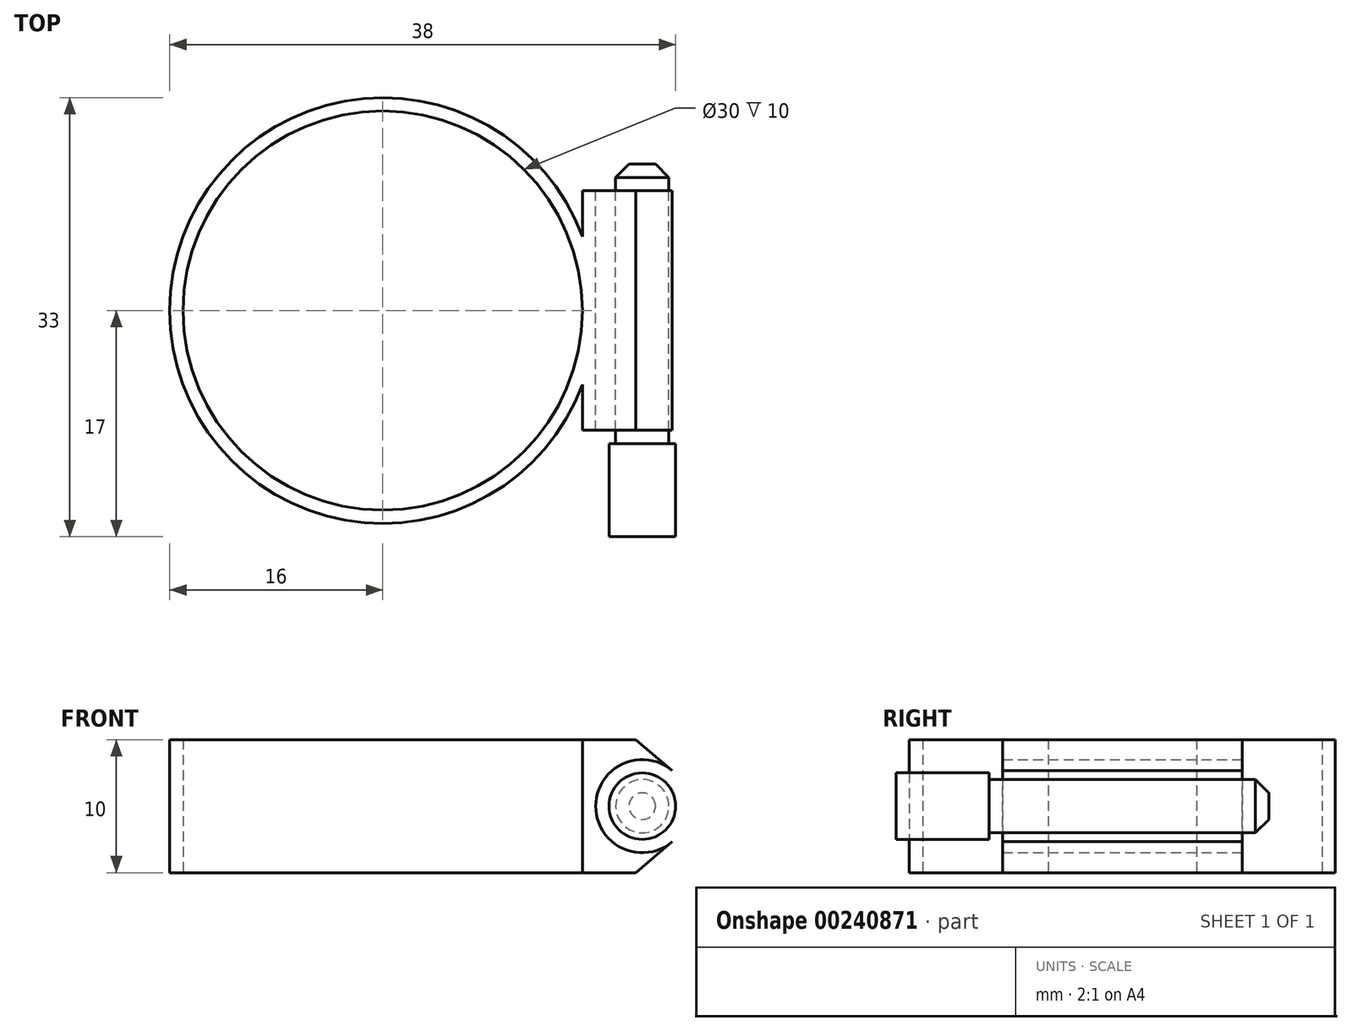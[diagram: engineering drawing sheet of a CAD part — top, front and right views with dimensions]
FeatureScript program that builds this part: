
annotation { "Feature Type Name" : "Feature", "Feature Type Description" : "" }
export const myFeature = defineFeature(function(context is Context, id is Id, definition is map)
    precondition{}
    {
        {
            var Q0;
            Q0=qCreatedBy(makeId("Front.planeOp"),FACE);
            var sketch = newSketch(context, id + "F0", { "sketchPlane" : qUnion([Q0])});
            skLineSegment(sketch, "E0.bottom", {"start": v(15, 0) * mm, "end": v(16, 0) * mm});
            skLineSegment(sketch, "E0.top", {"start": v(15, 10) * mm, "end": v(16, 10) * mm});
            skLineSegment(sketch, "E0.left", {"start": v(15, 0) * mm, "end": v(15, 10) * mm});
            skLineSegment(sketch, "E0.right", {"start": v(16, 0) * mm, "end": v(16, 10) * mm});
            skLineSegment(sketch, "E1", {"start": v(15, 5) * mm, "end": v(23, 5) * mm, "construction": true});
            skCircle(sketch, "E2", {"center": v(19.5, 5) * mm, "radius": 3.5 * mm});
            skLineSegment(sketch, "E3", {"start": v(16, 10) * mm, "end": v(19, 10) * mm});
            skLineSegment(sketch, "E4", {"start": v(19, 10) * mm, "end": v(21.76, 7.68) * mm});
            skPoint(sketch, "E5", {"position": v(16, 5) * mm});
            skLineSegment(sketch, "E6.MirrorCS", {"start": v(16, 0) * mm, "end": v(19, 0) * mm});
            skLineSegment(sketch, "E7.MirrorCS", {"start": v(19, 0) * mm, "end": v(21.76, 2.32) * mm});
            skLineSegment(sketch, "E8", {"start": v(0, 0) * mm, "end": v(0, 10) * mm, "construction": true});
            skSolve(sketch);
        }
        {
            var Q0;
            Q0=sQuery(id+"F0.wireOp",VERTEX,"E2.center");
            var Q1;
            Q1=qCreatedBy(makeId("Top.planeOp"),FACE);
            cPlane(context, id + "F1", {"entities" : qUnion([Q0, Q1]), "cplaneType" : CPlaneType.PLANE_POINT, "offset" : 25 * mm, "width" : 150 * mm, "height" : 150 * mm});
        }
        {
            var Q0;
            Q0=qCreatedBy(id+"F1.planeOp",FACE);
            var sketch = newSketch(context, id + "F2", { "sketchPlane" : qUnion([Q0])});
            skLineSegment(sketch, "E9", {"start": v(19.5, 11) * mm, "end": v(19.5, -17) * mm});
            skLineSegment(sketch, "E10", {"start": v(17.5, 10) * mm, "end": v(17.5, -10) * mm});
            skLineSegment(sketch, "E11", {"start": v(17.5, 10) * mm, "end": v(18.5, 11) * mm});
            skLineSegment(sketch, "E12", {"start": v(18.5, 11) * mm, "end": v(19.5, 11) * mm});
            skLineSegment(sketch, "E13", {"start": v(17.5, -10) * mm, "end": v(17, -10) * mm});
            skLineSegment(sketch, "E14", {"start": v(17, -10) * mm, "end": v(17, -17) * mm});
            skLineSegment(sketch, "E15", {"start": v(17, -17) * mm, "end": v(19.5, -17) * mm});
            skLineSegment(sketch, "E16", {"start": v(16, 9) * mm, "end": v(16, -9) * mm, "construction": true});
            skLineSegment(sketch, "E17", {"start": v(16, 9) * mm, "end": v(19.5, 9) * mm, "construction": true});
            skLineSegment(sketch, "E18", {"start": v(16, -9) * mm, "end": v(19.5, -9) * mm, "construction": true});
            skSolve(sketch);
        }
        {
            var Q0;
            Q0=makeQuery(id+"F2.imprint","IMPRINT",FACE,{"disambiguationData":[TD([[makeQuery(id+"F2.imprint","IMPRINT",EDGE,{"derivedFrom":sQuery(id+"F2.wireOp",EDGE,"E9")}),-1.0]])]});
            var Q1;
            Q1=sQuery(id+"F2.wireOp",EDGE,"E9");
            revolve(context, id + "F3", {"entities" : qUnion([Q0]), "axis" : qUnion([Q1]), "revolveType" : RevolveType.FULL});
        }
        {
            var Q0;
            {var subQ1=sQuery(id+"F0.wireOp",EDGE,"E0.bottom");Q0=makeQuery(id+"F0.imprint","IMPRINT",FACE,{"disambiguationData":[TD([[makeQuery(id+"F0.imprint","IMPRINT",EDGE,{"derivedFrom":subQ1}),1.0]])]});}
            var Q1;
            {var subQ0=sQuery(id+"F0.wireOp",EDGE,"E3");Q1=makeQuery(id+"F0.imprint","IMPRINT",FACE,{"disambiguationData":[TD([[makeQuery(id+"F0.imprint","IMPRINT",EDGE,{"derivedFrom":subQ0}),-1.0]])]});}
            var Q2;
            {var subQ0=sQuery(id+"F0.wireOp",EDGE,"E6.MirrorCS");Q2=makeQuery(id+"F0.imprint","IMPRINT",FACE,{"disambiguationData":[TD([[makeQuery(id+"F0.imprint","IMPRINT",EDGE,{"derivedFrom":subQ0}),1.0]])]});}
            var Q3;
            {var subQ0=sQuery(id+"F0.wireOp",EDGE,"E2");var subQ1=makeQuery(id+"F0.imprint","INTERSECT",VERTEX,{"derivedFrom":[subQ0,sQuery(id+"F0.wireOp",EDGE,"E7.MirrorCS")]});Q3=makeQuery(id+"F0.imprint","IMPRINT",FACE,{"disambiguationData":[TD([[makeQuery(id+"F0.imprint","IMPRINT",EDGE,{"disambiguationData":[TD([[subQ1,-1.0]])],"derivedFrom":subQ0}),-1.0]])]});}
            var Q4;
            Q4=sQuery(id+"F2.wireOp",VERTEX,"E16.end");
            var Q5;
            Q5=sQuery(id+"F2.wireOp",VERTEX,"E17.start");
            extrude(context, id + "F4", {"entities" : qUnion([Q0, Q1, Q2, Q3]), "operationType" : NewBodyOperationType.ADD, "endBound" : BoundingType.UP_TO_VERTEX, "endBoundEntityVertex" : qUnion([Q4]), "depth" : 25 * mm, "hasSecondDirection" : true, "secondDirectionBound" : SecondDirectionBoundingType.UP_TO_VERTEX, "secondDirectionOppositeDirection" : true, "secondDirectionBoundEntityVertex" : qUnion([Q5]), "secondDirectionDepth" : 25 * mm});
        }
        {
            var Q0;
            {var subQ1=sQuery(id+"F0.wireOp",EDGE,"E0.bottom");Q0=makeQuery(id+"F0.imprint","IMPRINT",FACE,{"disambiguationData":[TD([[makeQuery(id+"F0.imprint","IMPRINT",EDGE,{"derivedFrom":subQ1}),1.0]])]});}
            var Q1;
            Q1=sQuery(id+"F0.wireOp",EDGE,"E8");
            revolve(context, id + "F5", {"operationType" : NewBodyOperationType.ADD, "entities" : qUnion([Q0]), "axis" : qUnion([Q1]), "revolveType" : RevolveType.FULL});
        }
    });
